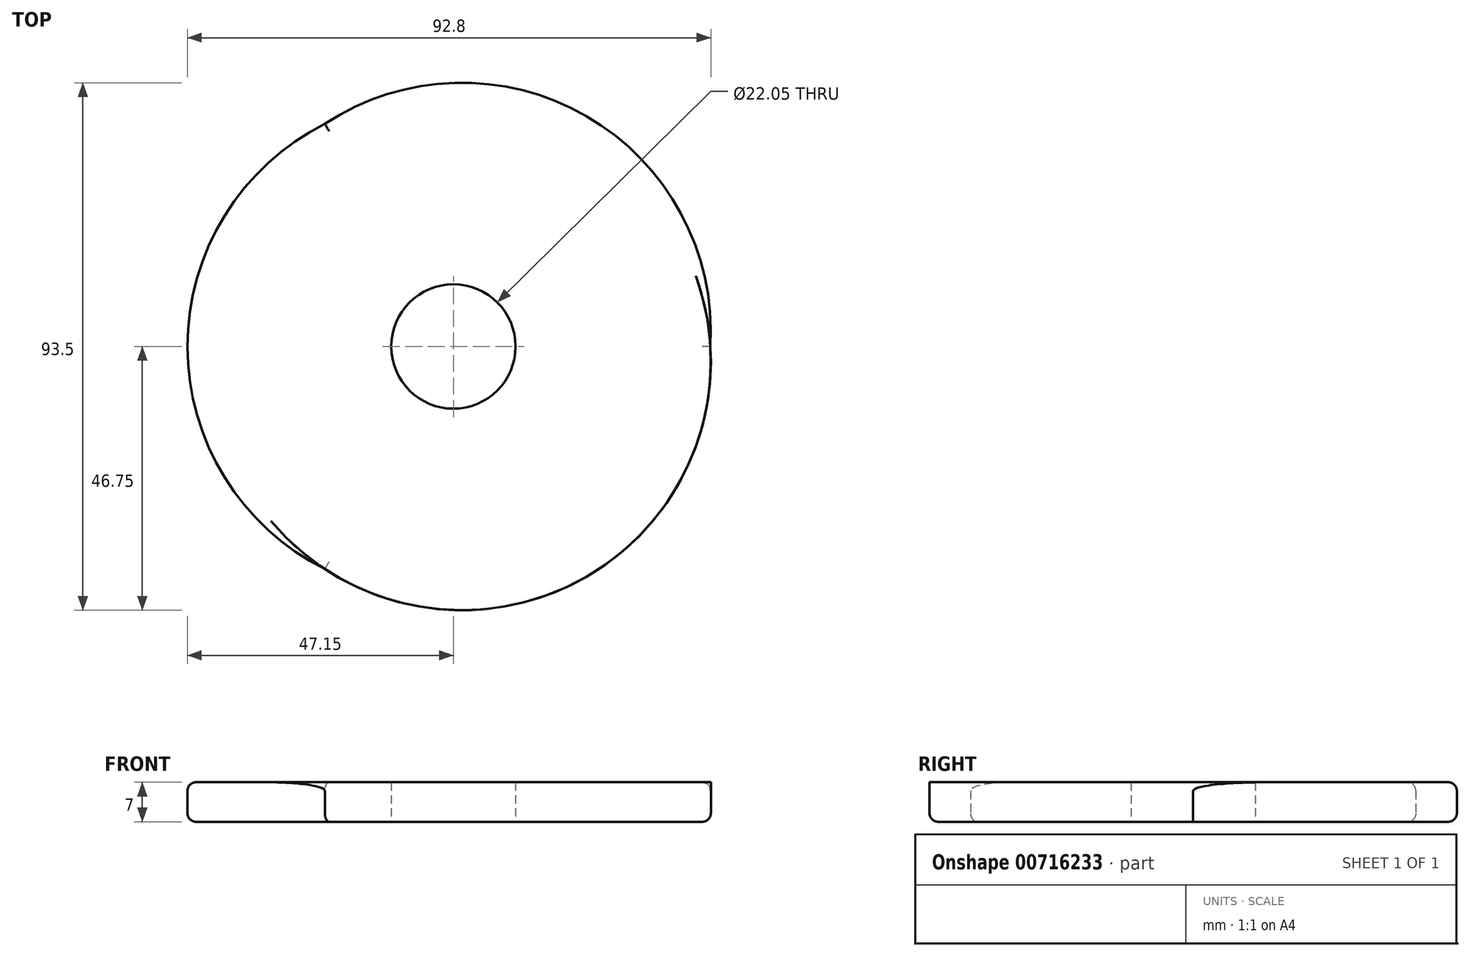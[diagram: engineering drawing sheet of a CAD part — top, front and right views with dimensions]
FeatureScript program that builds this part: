
annotation { "Feature Type Name" : "Feature", "Feature Type Description" : "" }
export const myFeature = defineFeature(function(context is Context, id is Id, definition is map)
    precondition{}
    {
        {
            var Q0;
            Q0=qCreatedBy(makeId("Top.planeOp"),FACE);
            var sketch = newSketch(context, id + "F0", { "sketchPlane" : qUnion([Q0])});
            skLineSegment(sketch, "E0.bottom", {"start": v(0, 0) * mm, "end": v(28, 0) * mm});
            skLineSegment(sketch, "E0.top", {"start": v(0, 30) * mm, "end": v(28, 30) * mm});
            skLineSegment(sketch, "E0.left", {"start": v(0, 0) * mm, "end": v(0, 30) * mm, "construction": true});
            skLineSegment(sketch, "E0.right", {"start": v(28, 0) * mm, "end": v(28, 30) * mm, "construction": true});
            skCircle(sketch, "E1", {"center": v(14, 0) * mm, "radius": 14 * mm});
            skCircle(sketch, "E2", {"center": v(14, 30) * mm, "radius": 14 * mm});
            skCircle(sketch, "E3", {"center": v(14, 0) * mm, "radius": 11.03 * mm});
            skCircle(sketch, "E4", {"center": v(14, 30) * mm, "radius": 11.03 * mm});
            skLineSegment(sketch, "E5", {"start": v(14, 30) * mm, "end": v(14, 0) * mm, "construction": true});
            skPoint(sketch, "E6.first.point", {"position": v(14, 16) * mm});
            skPoint(sketch, "E6.first.point.positionSnap0", {"position": v(14, 15) * mm});
            skLineSegment(sketch, "E7", {"start": v(0, 30) * mm, "end": v(14, 30) * mm, "construction": true});
            skLineSegment(sketch, "E8", {"start": v(7, 30) * mm, "end": v(7, 0) * mm, "construction": true});
            skLineSegment(sketch, "E9", {"start": v(0, 0) * mm, "end": v(14, 0) * mm});
            skLineSegment(sketch, "E10", {"start": v(14, 30) * mm, "end": v(28, 30) * mm, "construction": true});
            skLineSegment(sketch, "E11", {"start": v(14, 0) * mm, "end": v(28, 0) * mm});
            skLineSegment(sketch, "E12", {"start": v(21, 0) * mm, "end": v(21, 30) * mm, "construction": true});
            skLineSegment(sketch, "E13", {"start": v(28, 15) * mm, "end": v(28, 0) * mm, "construction": true});
            skLineSegment(sketch, "E14", {"start": v(28, 7.5) * mm, "end": v(0, 7.5) * mm, "construction": true});
            skLineSegment(sketch, "E15", {"start": v(0, 30) * mm, "end": v(0, 15) * mm, "construction": true});
            skLineSegment(sketch, "E16", {"start": v(0, 22.5) * mm, "end": v(28, 22.5) * mm, "construction": true});
            skPoint(sketch, "E17.first.point", {"position": v(7, 15) * mm});
            skCircle(sketch, "E18", {"center": v(1.43, 15) * mm, "radius": 5.57 * mm});
            skPoint(sketch, "E19", {"position": v(21, 15) * mm});
            skCircle(sketch, "E20", {"center": v(26.57, 15) * mm, "radius": 5.57 * mm});
            skCircle(sketch, "E21", {"center": v(11, 0) * mm, "radius": 44.15 * mm});
            skCircle(sketch, "E22", {"center": v(36.26, 3.44) * mm, "radius": 20.65 * mm});
            skSolve(sketch);
        }
        {
            var Q0;
            {var subQ1=sQuery(id+"F0.wireOp",EDGE,"E0.bottom");var subQ3=sQuery(id+"F0.wireOp",EDGE,"E3");var subQ4=makeQuery(id+"F0.imprint","INTERSECT",VERTEX,{"disambiguationData":[OD(0.0)],"derivedFrom":[subQ1,subQ3]});Q0=makeQuery(id+"F0.imprint","IMPRINT",FACE,{"disambiguationData":[TD([[makeQuery(id+"F0.imprint","IMPRINT",EDGE,{"disambiguationData":[TD([[subQ4,-1.0]])],"derivedFrom":subQ3}),-1.0]])]});}
            var Q1;
            {var subQ1=sQuery(id+"F0.wireOp",EDGE,"E0.bottom");var subQ3=sQuery(id+"F0.wireOp",EDGE,"E3");var subQ4=makeQuery(id+"F0.imprint","INTERSECT",VERTEX,{"disambiguationData":[OD(0.0)],"derivedFrom":[subQ1,subQ3]});Q1=makeQuery(id+"F0.imprint","IMPRINT",FACE,{"disambiguationData":[TD([[makeQuery(id+"F0.imprint","IMPRINT",EDGE,{"disambiguationData":[TD([[subQ4,1.0]])],"derivedFrom":subQ3}),-1.0]])]});}
            var Q2;
            {var subQ1=sQuery(id+"F0.wireOp",EDGE,"E0.left");var subQ3=sQuery(id+"F0.wireOp",EDGE,"E6");var subQ4=makeQuery(id+"F0.imprint","INTERSECT",VERTEX,{"derivedFrom":[subQ1,subQ3]});Q2=makeQuery(id+"F0.imprint","IMPRINT",FACE,{"disambiguationData":[TD([[makeQuery(id+"F0.imprint","IMPRINT",EDGE,{"disambiguationData":[TD([[subQ4,1.0]])],"derivedFrom":subQ3}),-1.0]])]});}
            var Q3;
            {var subQ1=sQuery(id+"F0.wireOp",EDGE,"E0.right");var subQ3=sQuery(id+"F0.wireOp",EDGE,"E6");var subQ4=makeQuery(id+"F0.imprint","INTERSECT",VERTEX,{"derivedFrom":[subQ1,subQ3]});Q3=makeQuery(id+"F0.imprint","IMPRINT",FACE,{"disambiguationData":[TD([[makeQuery(id+"F0.imprint","IMPRINT",EDGE,{"disambiguationData":[TD([[subQ4,-1.0]])],"derivedFrom":subQ3}),-1.0]])]});}
            var Q4;
            {var subQ0=sQuery(id+"F0.wireOp",EDGE,"E6");var subQ1=sQuery(id+"F0.wireOp",EDGE,"E2");var subQ2=makeQuery(id+"F0.imprint","INTERSECT",VERTEX,{"disambiguationData":[OD(0.0)],"derivedFrom":[subQ1,subQ0]});Q4=makeQuery(id+"F0.imprint","IMPRINT",FACE,{"disambiguationData":[TD([[makeQuery(id+"F0.imprint","IMPRINT",EDGE,{"disambiguationData":[TD([[subQ2,-1.0]])],"derivedFrom":subQ1}),-1.0]])]});}
            var Q5;
            {var subQ1=sQuery(id+"F0.wireOp",EDGE,"E0.top");var subQ4=sQuery(id+"F0.wireOp",EDGE,"E4");var subQ7=makeQuery(id+"F0.imprint","INTERSECT",VERTEX,{"disambiguationData":[OD(0.0)],"derivedFrom":[subQ1,subQ4]});Q5=makeQuery(id+"F0.imprint","IMPRINT",FACE,{"disambiguationData":[TD([[makeQuery(id+"F0.imprint","IMPRINT",EDGE,{"disambiguationData":[TD([[subQ7,1.0]])],"derivedFrom":subQ4}),-1.0]])]});}
            var Q6;
            {var subQ0=sQuery(id+"F0.wireOp",EDGE,"E2");var subQ5=sQuery(id+"F0.wireOp",EDGE,"iXxyTF50-2ilh-IIc2-Kw3h-GMxnBfHTMSWx");var subQ7=makeQuery(id+"F0.imprint","INTERSECT",VERTEX,{"derivedFrom":[subQ0,subQ5]});Q6=makeQuery(id+"F0.imprint","IMPRINT",FACE,{"disambiguationData":[TD([[makeQuery(id+"F0.imprint","IMPRINT",EDGE,{"disambiguationData":[TD([[subQ7,1.0]])],"derivedFrom":subQ5}),1.0]])]});}
            var Q7;
            {var subQ1=sQuery(id+"F0.wireOp",EDGE,"E0.top");var subQ5=sQuery(id+"F0.wireOp",EDGE,"E4");var subQ9=makeQuery(id+"F0.imprint","INTERSECT",VERTEX,{"disambiguationData":[OD(0.0)],"derivedFrom":[subQ1,subQ5]});Q7=makeQuery(id+"F0.imprint","IMPRINT",FACE,{"disambiguationData":[TD([[makeQuery(id+"F0.imprint","IMPRINT",EDGE,{"disambiguationData":[TD([[subQ9,-1.0]])],"derivedFrom":subQ5}),-1.0]])]});}
            var Q8;
            {var subQ0=sQuery(id+"F0.wireOp",EDGE,"E6");var subQ1=sQuery(id+"F0.wireOp",EDGE,"E2");var subQ2=makeQuery(id+"F0.imprint","INTERSECT",VERTEX,{"disambiguationData":[OD(0.0)],"derivedFrom":[subQ1,subQ0]});Q8=makeQuery(id+"F0.imprint","IMPRINT",FACE,{"disambiguationData":[TD([[makeQuery(id+"F0.imprint","IMPRINT",EDGE,{"disambiguationData":[TD([[subQ2,-1.0]])],"derivedFrom":subQ1}),1.0]])]});}
            var Q9;
            {var subQ3=sQuery(id+"F0.wireOp",EDGE,"E11");var subQ5=sQuery(id+"F0.wireOp",EDGE,"E1");var subQ6=makeQuery(id+"F0.imprint","INTERSECT",VERTEX,{"derivedFrom":[subQ5,subQ3]});Q9=makeQuery(id+"F0.imprint","IMPRINT",FACE,{"disambiguationData":[TD([[makeQuery(id+"F0.imprint","IMPRINT",EDGE,{"disambiguationData":[TD([[subQ6,-1.0]])],"derivedFrom":subQ5}),1.0]])]});}
            var Q10;
            {var subQ0=sQuery(id+"F0.wireOp",EDGE,"E20");var subQ1=sQuery(id+"F0.wireOp",EDGE,"E1");var subQ2=makeQuery(id+"F0.imprint","INTERSECT",VERTEX,{"derivedFrom":[subQ1,subQ0]});Q10=makeQuery(id+"F0.imprint","IMPRINT",FACE,{"disambiguationData":[TD([[makeQuery(id+"F0.imprint","IMPRINT",EDGE,{"disambiguationData":[TD([[subQ2,-1.0]])],"derivedFrom":subQ1}),-1.0]])]});}
            var Q11;
            {var subQ0=sQuery(id+"F0.wireOp",EDGE,"E9");var subQ1=sQuery(id+"F0.wireOp",EDGE,"E1");var subQ2=makeQuery(id+"F0.imprint","INTERSECT",VERTEX,{"derivedFrom":[subQ1,subQ0]});Q11=makeQuery(id+"F0.imprint","IMPRINT",FACE,{"disambiguationData":[TD([[makeQuery(id+"F0.imprint","IMPRINT",EDGE,{"disambiguationData":[TD([[subQ2,-1.0]])],"derivedFrom":subQ1}),1.0]])]});}
            var Q12;
            {var subQ0=sQuery(id+"F0.wireOp",EDGE,"E11");var subQ1=sQuery(id+"F0.wireOp",EDGE,"E1");var subQ2=makeQuery(id+"F0.imprint","INTERSECT",VERTEX,{"derivedFrom":[subQ1,subQ0]});Q12=makeQuery(id+"F0.imprint","IMPRINT",FACE,{"disambiguationData":[TD([[makeQuery(id+"F0.imprint","IMPRINT",EDGE,{"disambiguationData":[TD([[subQ2,1.0]])],"derivedFrom":subQ1}),1.0]])]});}
            var Q13;
            {var subQ1=sQuery(id+"F0.wireOp",EDGE,"E1");var subQ6=sQuery(id+"F0.wireOp",EDGE,"E22");var subQ8=makeQuery(id+"F0.imprint","INTERSECT",VERTEX,{"disambiguationData":[OD(0.0)],"derivedFrom":[subQ1,subQ6]});Q13=makeQuery(id+"F0.imprint","IMPRINT",FACE,{"disambiguationData":[TD([[makeQuery(id+"F0.imprint","IMPRINT",EDGE,{"disambiguationData":[TD([[subQ8,-1.0]])],"derivedFrom":subQ1}),1.0]])]});}
            var Q14;
            {var subQ0=sQuery(id+"F0.wireOp",EDGE,"E22");var subQ1=sQuery(id+"F0.wireOp",EDGE,"E1");var subQ2=makeQuery(id+"F0.imprint","INTERSECT",VERTEX,{"disambiguationData":[OD(0.0)],"derivedFrom":[subQ1,subQ0]});Q14=makeQuery(id+"F0.imprint","IMPRINT",FACE,{"disambiguationData":[TD([[makeQuery(id+"F0.imprint","IMPRINT",EDGE,{"disambiguationData":[TD([[subQ2,-1.0]])],"derivedFrom":subQ1}),-1.0]])]});}
            var Q15;
            {var subQ0=sQuery(id+"F0.wireOp",EDGE,"E2");var subQ1=makeQuery(id+"F0.imprint","INTERSECT",VERTEX,{"disambiguationData":[OD(1.0)],"derivedFrom":[sQuery(id+"F0.wireOp",EDGE,"E0.top"),subQ0]});Q15=makeQuery(id+"F0.imprint","IMPRINT",FACE,{"disambiguationData":[TD([[makeQuery(id+"F0.imprint","IMPRINT",EDGE,{"disambiguationData":[TD([[subQ1,-1.0]])],"derivedFrom":subQ0}),-1.0]])]});}
            extrude(context, id + "F1", {"entities" : qUnion([Q0, Q1, Q2, Q3, Q4, Q5, Q6, Q7, Q8, Q9, Q10, Q11, Q12, Q13, Q14, Q15]), "depth" : 7 * mm, "offsetDistance" : 25 * mm});
        }
        {
            var Q0;
            Q0=makeQuery(id+"F1.opExtrude","SWEPT_BODY",BODY,{"disambiguationData":[OSD([sQuery(id+"F0.wireOp",EDGE,"E0.left"),sQuery(id+"F0.wireOp",EDGE,"E0.right"),sQuery(id+"F0.wireOp",EDGE,"E1"),sQuery(id+"F0.wireOp",EDGE,"E2"),sQuery(id+"F0.wireOp",EDGE,"E3"),sQuery(id+"F0.wireOp",EDGE,"E4"),sQuery(id+"F0.wireOp",EDGE,"iXxyTF50-2ilh-IIc2-Kw3h-GMxnBfHTMSWx"),sQuery(id+"F0.wireOp",EDGE,"E6")])]});
            var Q1;
            Q1=makeQuery(id+"F1.opExtrude","SWEPT_FACE",FACE,{"disambiguationData":[OSD([sQuery(id+"F0.wireOp",EDGE,"E1")])]});
            circularPattern(context, id + "F2", {"operationType" : NewBodyOperationType.ADD, "entities" : qUnion([Q0]), "axis" : qUnion([Q1]), "angle" : 360 * degree, "instanceCount" : 3, "equalSpace" : true});
        }
        {
            var Q0;
            Q0=makeQuery(id+"F2.opPattern","COPY",EDGE,{"derivedFrom":makeQuery(id+"F1.opExtrude","CAP_EDGE",EDGE,{"disambiguationData":[OSD([sQuery(id+"F0.wireOp",EDGE,"E21")])],"isStart":false}),"instanceName":"1"});
            var Q1;
            Q1=makeQuery(id+"F2.opPattern","COPY",EDGE,{"derivedFrom":makeQuery(id+"F1.opExtrude","CAP_EDGE",EDGE,{"disambiguationData":[OSD([sQuery(id+"F0.wireOp",EDGE,"E22")])],"isStart":false}),"instanceName":"1"});
            var Q2;
            Q2=makeQuery(id+"F2.opPattern","COPY",EDGE,{"derivedFrom":makeQuery(id+"F1.opExtrude","CAP_EDGE",EDGE,{"disambiguationData":[OSD([sQuery(id+"F0.wireOp",EDGE,"E21")])],"isStart":true}),"instanceName":"1"});
            var Q3;
            Q3=makeQuery(id+"F1.opExtrude","CAP_EDGE",EDGE,{"disambiguationData":[OSD([sQuery(id+"F0.wireOp",EDGE,"E21")])],"isStart":false});
            var Q4;
            Q4=makeQuery(id+"F1.opExtrude","CAP_EDGE",EDGE,{"disambiguationData":[OSD([sQuery(id+"F0.wireOp",EDGE,"E21")])],"isStart":true});
            var Q5;
            Q5=makeQuery(id+"F2.opPattern","COPY",EDGE,{"derivedFrom":makeQuery(id+"F1.opExtrude","CAP_EDGE",EDGE,{"disambiguationData":[OSD([sQuery(id+"F0.wireOp",EDGE,"E22")])],"isStart":true}),"instanceName":"1"});
            var Q6;
            Q6=makeQuery(id+"F2.opPattern","COPY",EDGE,{"derivedFrom":makeQuery(id+"F1.opExtrude","CAP_EDGE",EDGE,{"disambiguationData":[OSD([sQuery(id+"F0.wireOp",EDGE,"E21")])],"isStart":true}),"instanceName":"2"});
            var Q7;
            Q7=makeQuery(id+"F2.opPattern","COPY",EDGE,{"derivedFrom":makeQuery(id+"F1.opExtrude","CAP_EDGE",EDGE,{"disambiguationData":[OSD([sQuery(id+"F0.wireOp",EDGE,"E2")])],"isStart":true}),"instanceName":"2"});
            fillet(context, id + "F3", {"entities" : qUnion([Q0, Q1, Q2, Q3, Q4, Q5, Q6, Q7]), "radius" : 1.5 * mm, "tangentPropagation" : true, "allowEdgeOverflow" : false});
        }
    });
